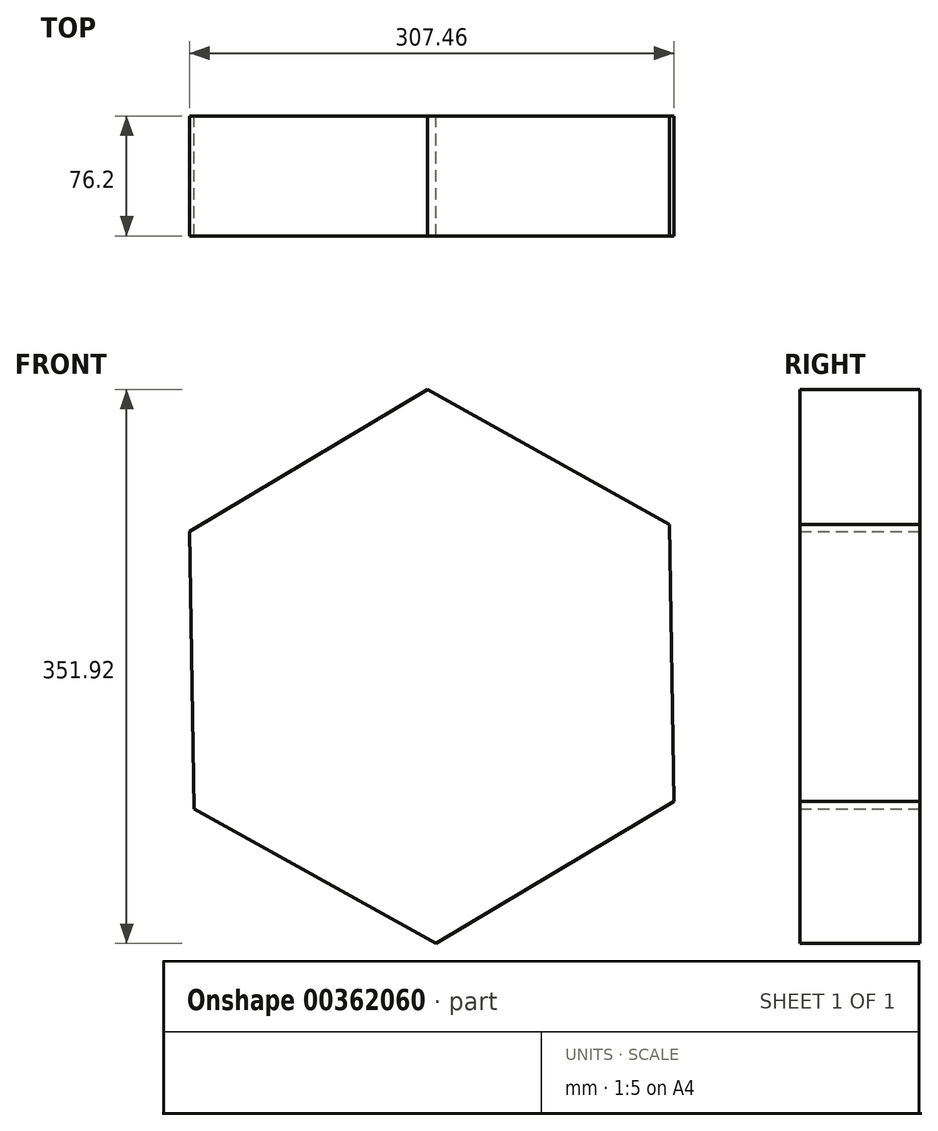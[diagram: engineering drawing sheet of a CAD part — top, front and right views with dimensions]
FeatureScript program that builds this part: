
annotation { "Feature Type Name" : "Feature", "Feature Type Description" : "" }
export const myFeature = defineFeature(function(context is Context, id is Id, definition is map)
    precondition{}
    {
        {
            var Q0;
            Q0=qCreatedBy(makeId("Front.planeOp"),FACE);
            var sketch = newSketch(context, id + "F0", { "sketchPlane" : qUnion([Q0])});
            skCircle(sketch, "E0", {"center": v(0, 0) * mm, "radius": 152.4 * mm});
            skCircle(sketch, "E1.cCircle", {"center": v(0, 0) * mm, "radius": 152.4 * mm, "construction": true});
            skLineSegment(sketch, "E1.0", {"start": v(-153.73, 85.65) * mm, "end": v(-2.7, 175.96) * mm});
            skLineSegment(sketch, "E1.1", {"start": v(-2.7, 175.96) * mm, "end": v(151.04, 90.31) * mm});
            skLineSegment(sketch, "E1.2", {"start": v(151.04, 90.31) * mm, "end": v(153.73, -85.65) * mm});
            skLineSegment(sketch, "E1.3", {"start": v(153.73, -85.65) * mm, "end": v(2.7, -175.96) * mm});
            skLineSegment(sketch, "E1.4", {"start": v(2.7, -175.96) * mm, "end": v(-151.04, -90.31) * mm});
            skLineSegment(sketch, "E1.5", {"start": v(-151.04, -90.31) * mm, "end": v(-153.73, 85.65) * mm});
            skPoint(sketch, "E1.0.midPoint", {"position": v(-78.21, 130.8) * mm});
            skSolve(sketch);
        }
        {
            var Q0;
            {var subQ0=sQuery(id+"F0.wireOp",EDGE,"E0");var subQ4=makeQuery(id+"F0.imprint","INTERSECT",VERTEX,{"derivedFrom":[subQ0,sQuery(id+"F0.wireOp",EDGE,"E1.1")]});Q0=makeQuery(id+"F0.imprint","IMPRINT",FACE,{"disambiguationData":[TD([[makeQuery(id+"F0.imprint","IMPRINT",EDGE,{"disambiguationData":[TD([[subQ4,1.0]])],"derivedFrom":subQ0}),1.0]])]});}
            var Q1;
            {var subQ0=sQuery(id+"F0.wireOp",EDGE,"E1.1");var subQ1=sQuery(id+"F0.wireOp",EDGE,"E0");var subQ2=makeQuery(id+"F0.imprint","INTERSECT",VERTEX,{"derivedFrom":[subQ1,subQ0]});Q1=makeQuery(id+"F0.imprint","IMPRINT",FACE,{"disambiguationData":[TD([[makeQuery(id+"F0.imprint","IMPRINT",EDGE,{"disambiguationData":[TD([[subQ2,-1.0]])],"derivedFrom":subQ1}),-1.0]])]});}
            var Q2;
            {var subQ0=sQuery(id+"F0.wireOp",EDGE,"E1.0");var subQ1=sQuery(id+"F0.wireOp",EDGE,"E0");var subQ2=makeQuery(id+"F0.imprint","INTERSECT",VERTEX,{"derivedFrom":[subQ1,subQ0]});Q2=makeQuery(id+"F0.imprint","IMPRINT",FACE,{"disambiguationData":[TD([[makeQuery(id+"F0.imprint","IMPRINT",EDGE,{"disambiguationData":[TD([[subQ2,-1.0]])],"derivedFrom":subQ1}),-1.0]])]});}
            var Q3;
            {var subQ0=sQuery(id+"F0.wireOp",EDGE,"E1.5");var subQ1=sQuery(id+"F0.wireOp",EDGE,"E0");var subQ2=makeQuery(id+"F0.imprint","INTERSECT",VERTEX,{"derivedFrom":[subQ1,subQ0]});Q3=makeQuery(id+"F0.imprint","IMPRINT",FACE,{"disambiguationData":[TD([[makeQuery(id+"F0.imprint","IMPRINT",EDGE,{"disambiguationData":[TD([[subQ2,-1.0]])],"derivedFrom":subQ1}),-1.0]])]});}
            var Q4;
            {var subQ0=sQuery(id+"F0.wireOp",EDGE,"E1.4");var subQ1=sQuery(id+"F0.wireOp",EDGE,"E0");var subQ2=makeQuery(id+"F0.imprint","INTERSECT",VERTEX,{"derivedFrom":[subQ1,subQ0]});Q4=makeQuery(id+"F0.imprint","IMPRINT",FACE,{"disambiguationData":[TD([[makeQuery(id+"F0.imprint","IMPRINT",EDGE,{"disambiguationData":[TD([[subQ2,-1.0]])],"derivedFrom":subQ1}),-1.0]])]});}
            var Q5;
            {var subQ0=sQuery(id+"F0.wireOp",EDGE,"E1.2");var subQ1=sQuery(id+"F0.wireOp",EDGE,"E0");var subQ2=makeQuery(id+"F0.imprint","INTERSECT",VERTEX,{"derivedFrom":[subQ1,subQ0]});Q5=makeQuery(id+"F0.imprint","IMPRINT",FACE,{"disambiguationData":[TD([[makeQuery(id+"F0.imprint","IMPRINT",EDGE,{"disambiguationData":[TD([[subQ2,1.0]])],"derivedFrom":subQ1}),-1.0]])]});}
            var Q6;
            {var subQ0=sQuery(id+"F0.wireOp",EDGE,"E1.1");var subQ1=sQuery(id+"F0.wireOp",EDGE,"E0");var subQ2=makeQuery(id+"F0.imprint","INTERSECT",VERTEX,{"derivedFrom":[subQ1,subQ0]});Q6=makeQuery(id+"F0.imprint","IMPRINT",FACE,{"disambiguationData":[TD([[makeQuery(id+"F0.imprint","IMPRINT",EDGE,{"disambiguationData":[TD([[subQ2,1.0]])],"derivedFrom":subQ1}),-1.0]])]});}
            extrude(context, id + "F1", {"entities" : qUnion([Q0, Q1, Q2, Q3, Q4, Q5, Q6]), "depth" : 76.2 * mm});
        }
    });
